# Revit family: Luna 12 Cord
name_source: partatom
category: Lighting Fixtures
revit_build: Autodesk Revit 2017 (Build: 20181011_1645(x64)
units: mm (PartAtom-declared; Revit-internal decimal feet)

## family parameters
Cut with Voids When Loaded = No
Host = Face
Light Source = Yes
Part Type = Normal
Room Calculation Point = No
Round Connector Dimension = Use Diameter
Shared = No

## types (1)
- True Black
    Canopy Width = 0' - 5"
    Color Filter = 16777215
    Cost = 259 $
    Default Elevation = 4' - 0"
    Description = Pared down to the elements of line and light, the Luna Collection retains a delicate, sculptural quality that illuminates a room even when unlit. A stylish take on task lighting, the glass shade’s milky finish imparts a moon-like glow. A vinyl cord and streamlined components add to the versatility and simplicity of this fixture. Manufactured in our Portland, Ore. factory to exacting specifications. A Schoolhouse Original.
    Dimming Lamp Color Temperature Shift = <None>
    Emit Shape Visible in Rendering = No
    Emit from Circle Diameter = 2' - 0"
    Height = 3' - 0"
    Lamp Shade Diameter = 1' - 0"
    Lamp Shade Radius = 0' - 6"
    Length Sub 1 = 0' - 6"
    Light Source Symbol Size = 2' - 0"
    Manufacturer = Schoolhouse
    Max Wattage = 60 W
    Model = Luna Rod Pendant with 12" Shade
    Primary Finishes = Schoolhouse Black 0-0-0
    Product Material = Brass
    URL = https://www.schoolhouse.com
    Voltage = 120 V

## geometry (parser evidence)
native form markers: Sweep x7
no freeform markers — native parametric forms only
